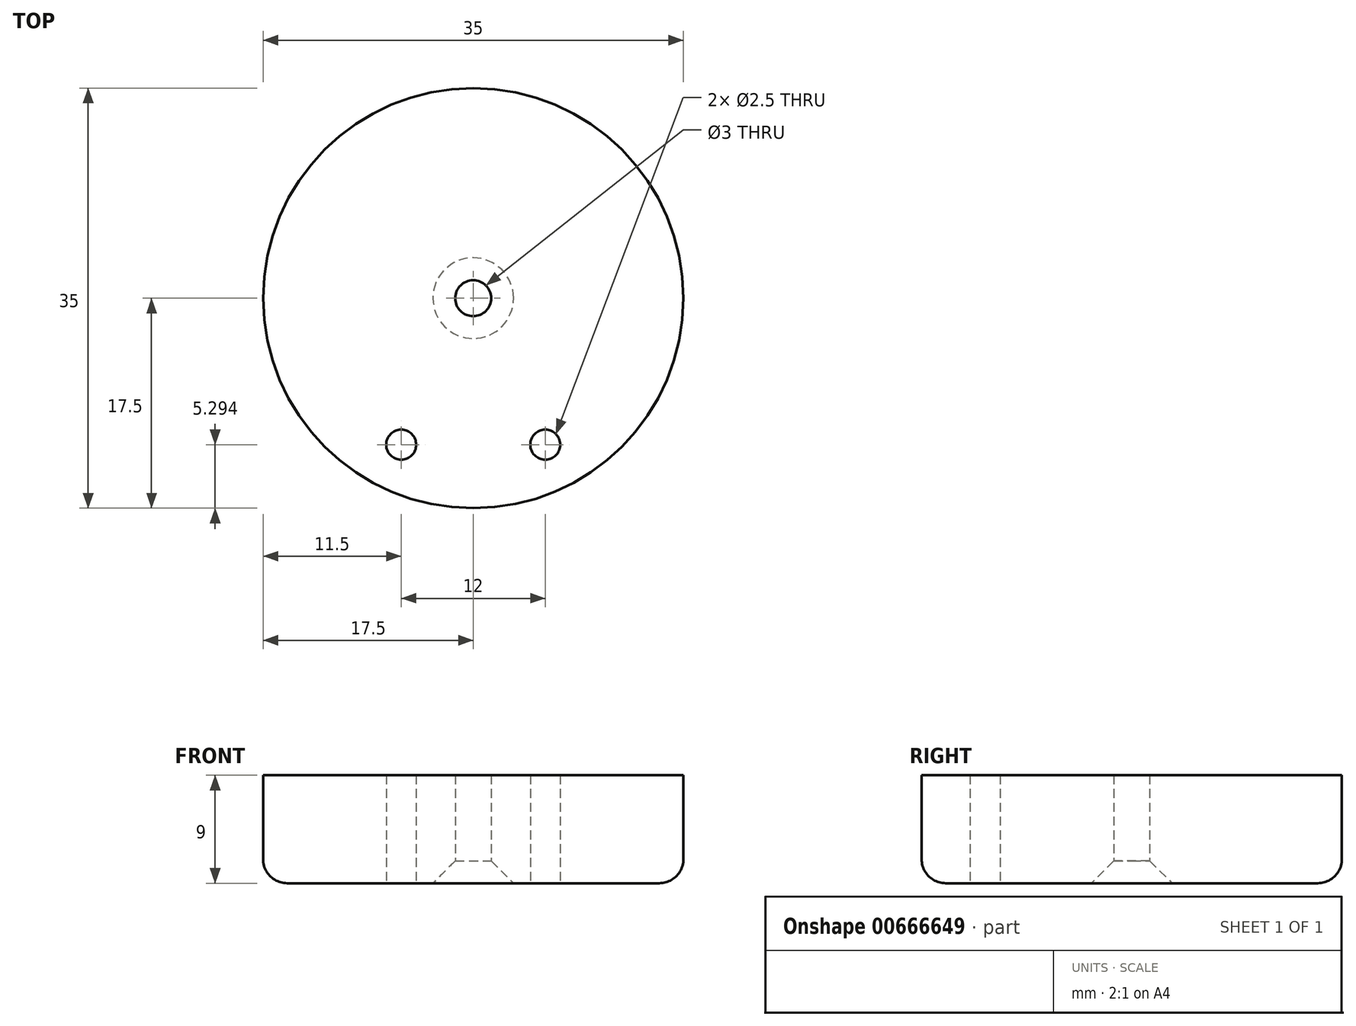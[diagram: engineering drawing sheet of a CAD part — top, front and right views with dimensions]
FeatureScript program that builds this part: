
annotation { "Feature Type Name" : "Feature", "Feature Type Description" : "" }
export const myFeature = defineFeature(function(context is Context, id is Id, definition is map)
    precondition{}
    {
        {
            var Q0;
            Q0=qCreatedBy(makeId("Top.planeOp"),FACE);
            var sketch = newSketch(context, id + "F0", { "sketchPlane" : qUnion([Q0])});
            skCircle(sketch, "E0", {"center": v(0, 0) * mm, "radius": 17.5 * mm});
            skLineSegment(sketch, "E1.bottom", {"start": v(-6, 12.2) * mm, "end": v(6, 12.2) * mm, "construction": true});
            skLineSegment(sketch, "E1.top", {"start": v(-6, -12.2) * mm, "end": v(6, -12.2) * mm, "construction": true});
            skLineSegment(sketch, "E1.left", {"start": v(-6, 12.2) * mm, "end": v(-6, -12.2) * mm, "construction": true});
            skLineSegment(sketch, "E1.right", {"start": v(6, 12.2) * mm, "end": v(6, -12.2) * mm, "construction": true});
            skSolve(sketch);
        }
        {
            var Q0;
            Q0=makeQuery(id+"F0.imprint","IMPRINT",FACE,{"disambiguationData":[TD([[makeQuery(id+"F0.imprint","IMPRINT",EDGE,{"derivedFrom":sQuery(id+"F0.wireOp",EDGE,"E0")}),1.0]])]});
            extrude(context, id + "F1", {"entities" : qUnion([Q0]), "depth" : 9 * mm, "offsetDistance" : 25 * mm});
        }
        {
            var Q0;
            Q0=sQuery(id+"F0.wireOp",VERTEX,"E0.center");
            var Q1;
            Q1=makeQuery(id+"F1.opExtrude","SWEPT_BODY",BODY,{"disambiguationData":[OSD([sQuery(id+"F0.wireOp",EDGE,"E0")])]});
            hole(context, id + "F2", {"style" : HoleStyle.C_SINK, "endStyle" : HoleEndStyle.THROUGH, "oppositeDirection" : true, "standardTappedOrClearance" : lookupTablePath({ "standard" : "ISO", "size" : "3", "type" : "Drilled" }), "standardBlindInLast" : lookupTablePath({ "standard" : "ISO", "size" : "3", "type" : "Drilled" }), "holeDiameter" : 3 * mm, "cSinkDiameter" : 6.72 * mm, "cSinkAngle" : 90 * degree, "majorDiameter" : 5 * mm, "isTappedThrough" : true, "tappedDepth" : 12 * mm, "tapClearance" : 3, "locations" : qUnion([Q0]), "scope" : qUnion([Q1])});
        }
        {
            var Q0;
            Q0=sQuery(id+"F0.wireOp",VERTEX,"E1.right.end");
            var Q1;
            Q1=sQuery(id+"F0.wireOp",VERTEX,"E1.left.end");
            var Q2;
            Q2=makeQuery(id+"F1.opExtrude","SWEPT_BODY",BODY,{"disambiguationData":[OSD([sQuery(id+"F0.wireOp",EDGE,"E0")])]});
            hole(context, id + "F3", {"style" : HoleStyle.SIMPLE, "endStyle" : HoleEndStyle.THROUGH, "oppositeDirection" : true, "holeDiameter" : 2.5 * mm, "majorDiameter" : 5 * mm, "isTappedThrough" : true, "tappedDepth" : 12 * mm, "tapClearance" : 3, "locations" : qUnion([Q0, Q1]), "scope" : qUnion([Q2])});
        }
        {
            var Q0;
            Q0=makeQuery(id+"F1.opExtrude","CAP_EDGE",EDGE,{"disambiguationData":[OSD([sQuery(id+"F0.wireOp",EDGE,"E0")])],"isStart":true});
            fillet(context, id + "F4", {"entities" : qUnion([Q0]), "radius" : 2 * mm, "tangentPropagation" : true, "allowEdgeOverflow" : false});
        }
        {
            var Q0;
            Q0=makeQuery(id+"F1.opExtrude","CAP_FACE",FACE,{"disambiguationData":[OSD([sQuery(id+"F0.wireOp",EDGE,"E0")])],"isStart":false});
            cPlane(context, id + "F5", {"entities" : qUnion([Q0]), "cplaneType" : CPlaneType.OFFSET, "offset" : 0 * mm, "width" : 150 * mm, "height" : 150 * mm});
        }
    });
